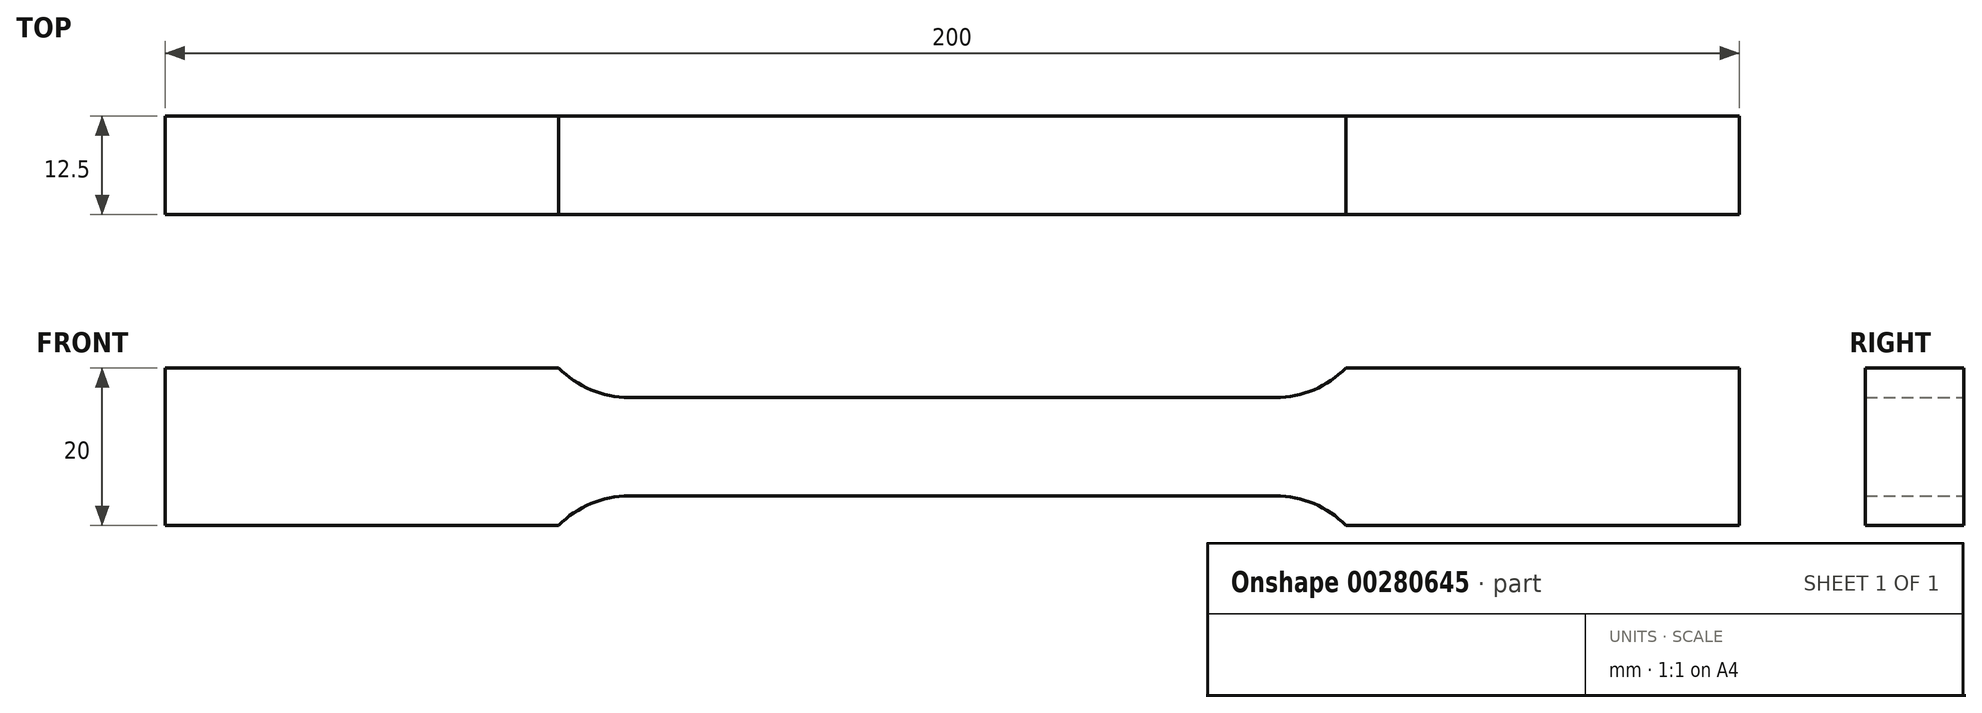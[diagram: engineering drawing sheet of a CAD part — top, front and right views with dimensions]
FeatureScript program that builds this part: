
annotation { "Feature Type Name" : "Feature", "Feature Type Description" : "" }
export const myFeature = defineFeature(function(context is Context, id is Id, definition is map)
    precondition{}
    {
        {
            var Q0;
            Q0=qCreatedBy(makeId("Front.planeOp"),FACE);
            var sketch = newSketch(context, id + "F0", { "sketchPlane" : qUnion([Q0])});
            skLineSegment(sketch, "E0", {"start": v(0, 6.25) * mm, "end": v(41.07, 6.25) * mm});
            skArc(sketch, "E1", {"start": v(41.07, 6.25) * mm, "mid": v(45.91, 7.23) * mm, "end": v(50, 10) * mm});
            skLineSegment(sketch, "E2", {"start": v(50, 10) * mm, "end": v(100, 10) * mm});
            skLineSegment(sketch, "E3", {"start": v(100, 10) * mm, "end": v(100, 0) * mm});
            skLineSegment(sketch, "E4.MirrorCS", {"start": v(0, -6.25) * mm, "end": v(41.07, -6.25) * mm});
            skArc(sketch, "E5.MirrorCS", {"start": v(41.07, -6.25) * mm, "mid": v(45.91, -7.23) * mm, "end": v(50, -10) * mm});
            skLineSegment(sketch, "E6.MirrorCS", {"start": v(100, -10) * mm, "end": v(100, 0) * mm});
            skLineSegment(sketch, "E7.MirrorCS", {"start": v(50, -10) * mm, "end": v(100, -10) * mm});
            skArc(sketch, "E8.MirrorCS", {"start": v(-41.07, 6.25) * mm, "mid": v(-45.91, 7.23) * mm, "end": v(-50, 10) * mm});
            skLineSegment(sketch, "E9.MirrorCS", {"start": v(-50, 10) * mm, "end": v(-100, 10) * mm});
            skArc(sketch, "E10.MirrorCS", {"start": v(-41.07, -6.25) * mm, "mid": v(-45.91, -7.23) * mm, "end": v(-50, -10) * mm});
            skLineSegment(sketch, "E11.MirrorCS", {"start": v(0, 6.25) * mm, "end": v(-41.07, 6.25) * mm});
            skLineSegment(sketch, "E12.MirrorCS", {"start": v(-100, -10) * mm, "end": v(-100, 0) * mm});
            skLineSegment(sketch, "E13.MirrorCS", {"start": v(0, -6.25) * mm, "end": v(-41.07, -6.25) * mm});
            skLineSegment(sketch, "E14.MirrorCS", {"start": v(-100, 10) * mm, "end": v(-100, 0) * mm});
            skLineSegment(sketch, "E15.MirrorCS", {"start": v(-50, -10) * mm, "end": v(-100, -10) * mm});
            skSolve(sketch);
        }
        {
            var Q0;
            Q0 = qSketchRegion(id + "F0", true);
            var Q1;
            Q1=sQuery(id+"F0.wireOp",EDGE,"E0");
            extrude(context, id + "F1", {"entities" : qUnion([Q0]), "surfaceEntities" : qUnion([Q1]), "endBound" : BoundingType.SYMMETRIC, "depth" : 12.5 * mm});
        }
    });
